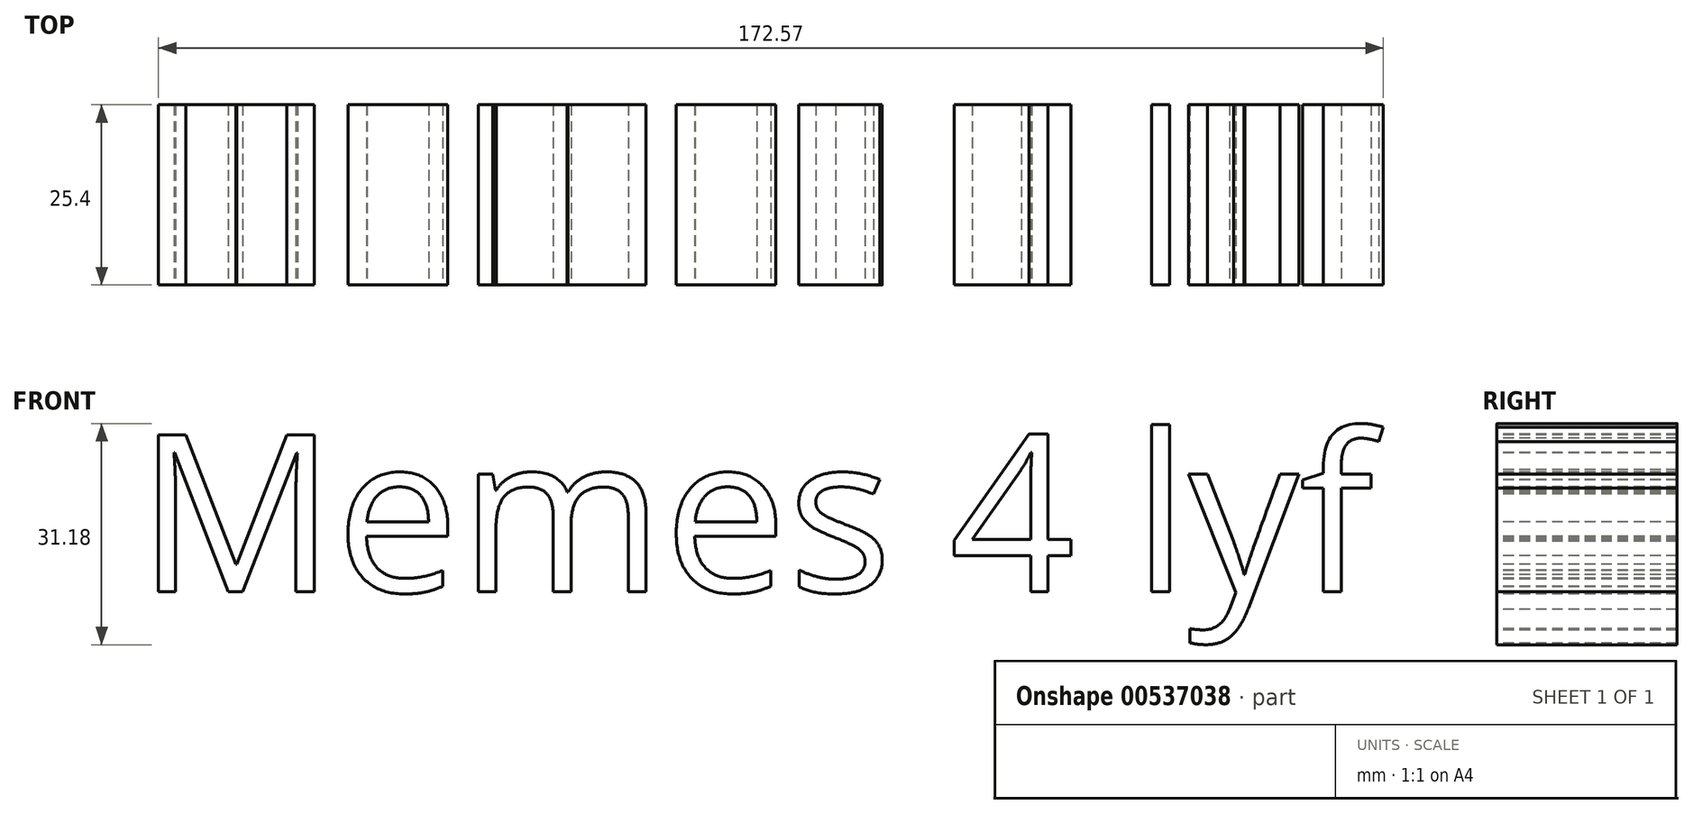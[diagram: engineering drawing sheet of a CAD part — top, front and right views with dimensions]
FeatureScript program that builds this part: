
annotation { "Feature Type Name" : "Feature", "Feature Type Description" : "" }
export const myFeature = defineFeature(function(context is Context, id is Id, definition is map)
    precondition{}
    {
        {
            var Q0;
            Q0=qCreatedBy(makeId("Front.planeOp"),FACE);
            var sketch = newSketch(context, id + "F0", { "sketchPlane" : qUnion([Q0])});
            skPoint(sketch, "E0.0", {"position": v(0, 0) * mm});
            skText(sketch, "E1", { "text": "Memes 4 lyf", "fontName": "OpenSans-Regular.ttf"});
            const initialGuessF0  = {"E1": [-0.04993, 0.01302, 1, 0, 0.02233]};
            skSetInitialGuess(sketch, initialGuessF0);
            skSolve(sketch);
        }
        {
            var Q0;
            Q0 = qConstructionFilter(qBodyType(qCreatedBy(id + "F0" ,EDGE), BodyType.WIRE), ConstructionObject.NO);
            extrude(context, id + "F1", {"bodyType" : ToolBodyType.SURFACE, "surfaceEntities" : qUnion([Q0]), "depth" : 25.4 * mm, "offsetDistance" : 25.4 * mm});
        }
    });
